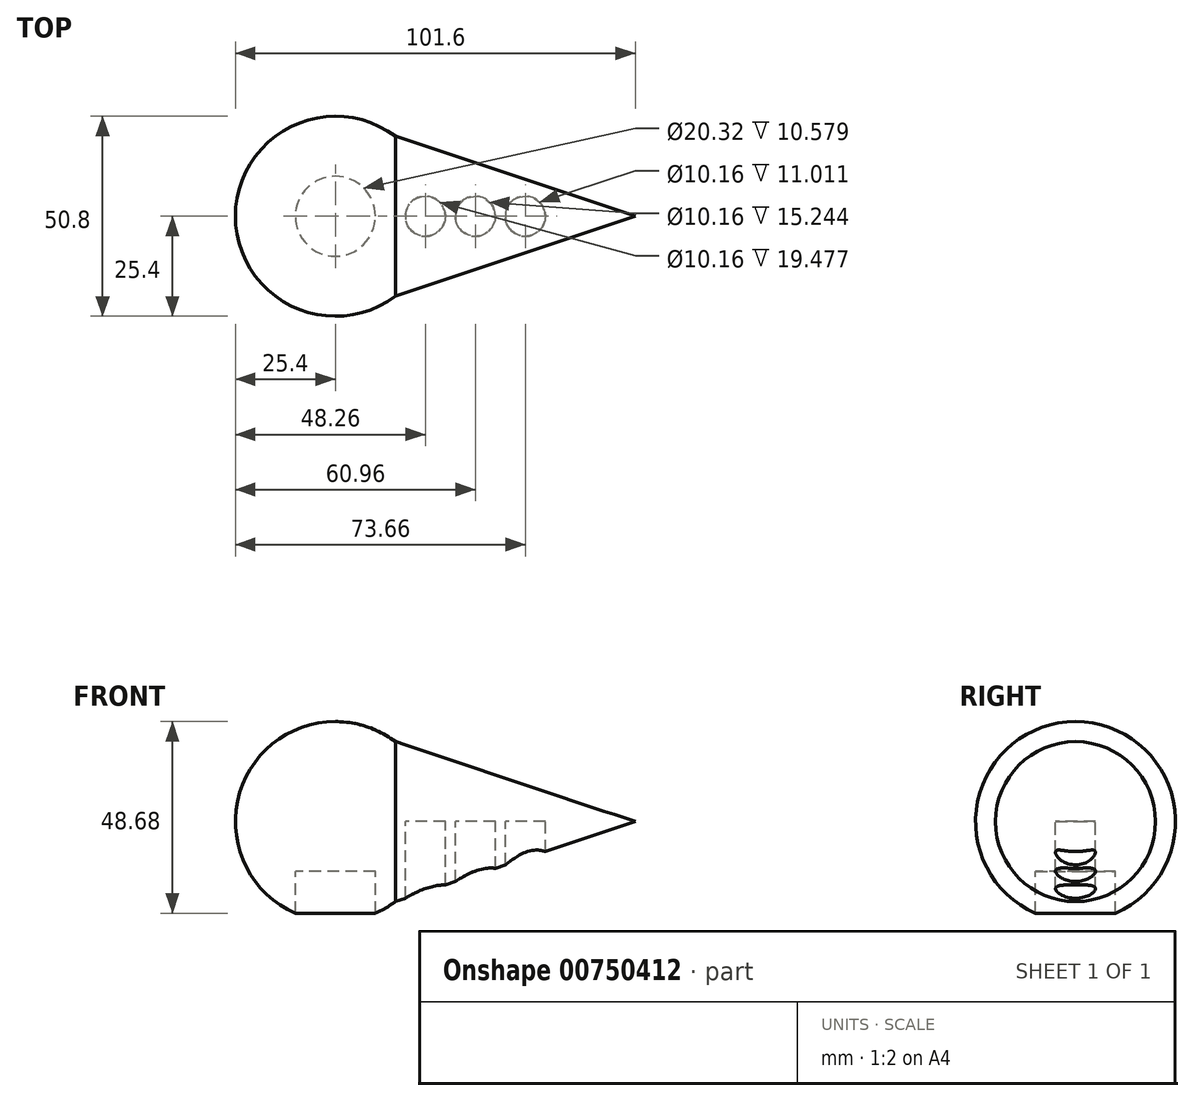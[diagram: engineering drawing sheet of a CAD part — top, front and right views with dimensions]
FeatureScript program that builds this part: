
annotation { "Feature Type Name" : "Feature", "Feature Type Description" : "" }
export const myFeature = defineFeature(function(context is Context, id is Id, definition is map)
    precondition{}
    {
        {
            var Q0;
            Q0=qCreatedBy(makeId("Front.planeOp"),FACE);
            var sketch = newSketch(context, id + "F0", { "sketchPlane" : qUnion([Q0])});
            skArc(sketch, "E0", {"start": v(0, 25.4) * mm, "mid": v(-25.4, 0) * mm, "end": v(0, -25.4) * mm});
            skLineSegment(sketch, "E1", {"start": v(0, 25.4) * mm, "end": v(0, -25.4) * mm});
            skSolve(sketch);
        }
        {
            var Q0;
            Q0=makeQuery(id+"F0.imprint","IMPRINT",FACE,{"disambiguationData":[TD([[makeQuery(id+"F0.imprint","IMPRINT",EDGE,{"derivedFrom":sQuery(id+"F0.wireOp",EDGE,"E0")}),1.0]])]});
            var Q1;
            Q1=sQuery(id+"F0.wireOp",EDGE,"E1");
            revolve(context, id + "F1", {"surfaceOperationType" : NewSurfaceOperationType.NEW, "entities" : qUnion([Q0]), "axis" : qUnion([Q1]), "revolveType" : RevolveType.FULL});
        }
        {
            var Q0;
            Q0=qCreatedBy(makeId("Front.planeOp"),FACE);
            var sketch = newSketch(context, id + "F2", { "sketchPlane" : qUnion([Q0])});
            skLineSegment(sketch, "E2.bottom", {"start": v(0, 0) * mm, "end": v(76.2, 0) * mm});
            skLineSegment(sketch, "E2.left", {"start": v(0, 0) * mm, "end": v(0, 25.4) * mm});
            skLineSegment(sketch, "E3", {"start": v(0, 25.4) * mm, "end": v(76.2, 0) * mm});
            skSolve(sketch);
        }
        {
            var Q0;
            Q0 = qSketchRegion(id + "F2", true);
            var Q1;
            Q1=sQuery(id+"F2.wireOp",EDGE,"E2.bottom");
            revolve(context, id + "F3", {"operationType" : NewBodyOperationType.ADD, "surfaceOperationType" : NewSurfaceOperationType.NEW, "entities" : qUnion([Q0]), "axis" : qUnion([Q1]), "revolveType" : RevolveType.FULL});
        }
        {
            var Q0;
            Q0=qCreatedBy(makeId("Top.planeOp"),FACE);
            var sketch = newSketch(context, id + "F4", { "sketchPlane" : qUnion([Q0])});
            skCircle(sketch, "E4", {"center": v(0, 0) * mm, "radius": 10.16 * mm});
            skSolve(sketch);
        }
        {
            var Q0;
            Q0 = qSketchRegion(id + "F4", true);
            extrude(context, id + "F5", {"entities" : qUnion([Q0]), "operationType" : NewBodyOperationType.REMOVE, "oppositeDirection" : true, "depth" : 25.4 * mm, "offsetDistance" : 25.4 * mm});
        }
        {
            var Q0;
            Q0=qCreatedBy(makeId("Top.planeOp"),FACE);
            var sketch = newSketch(context, id + "F6", { "sketchPlane" : qUnion([Q0])});
            skCircle(sketch, "E5", {"center": v(0, 0) * mm, "radius": 10.16 * mm});
            skSolve(sketch);
        }
        {
            var Q0;
            Q0 = qSketchRegion(id + "F6", true);
            extrude(context, id + "F7", {"entities" : qUnion([Q0]), "operationType" : NewBodyOperationType.ADD, "oppositeDirection" : true, "depth" : 12.7 * mm, "offsetDistance" : 25.4 * mm});
        }
        {
            var Q0;
            Q0=qCreatedBy(makeId("Top.planeOp"),FACE);
            var sketch = newSketch(context, id + "F8", { "sketchPlane" : qUnion([Q0])});
            skCircle(sketch, "E6", {"center": v(22.86, 0) * mm, "radius": 5.08 * mm});
            skCircle(sketch, "E7", {"center": v(35.56, 0) * mm, "radius": 5.08 * mm});
            skCircle(sketch, "E8", {"center": v(48.26, 0) * mm, "radius": 5.08 * mm});
            skSolve(sketch);
        }
        {
            var Q0;
            Q0 = qSketchRegion(id + "F8", true);
            extrude(context, id + "F9", {"entities" : qUnion([Q0]), "operationType" : NewBodyOperationType.REMOVE, "oppositeDirection" : true, "depth" : 25.4 * mm, "offsetDistance" : 25.4 * mm});
        }
    });
